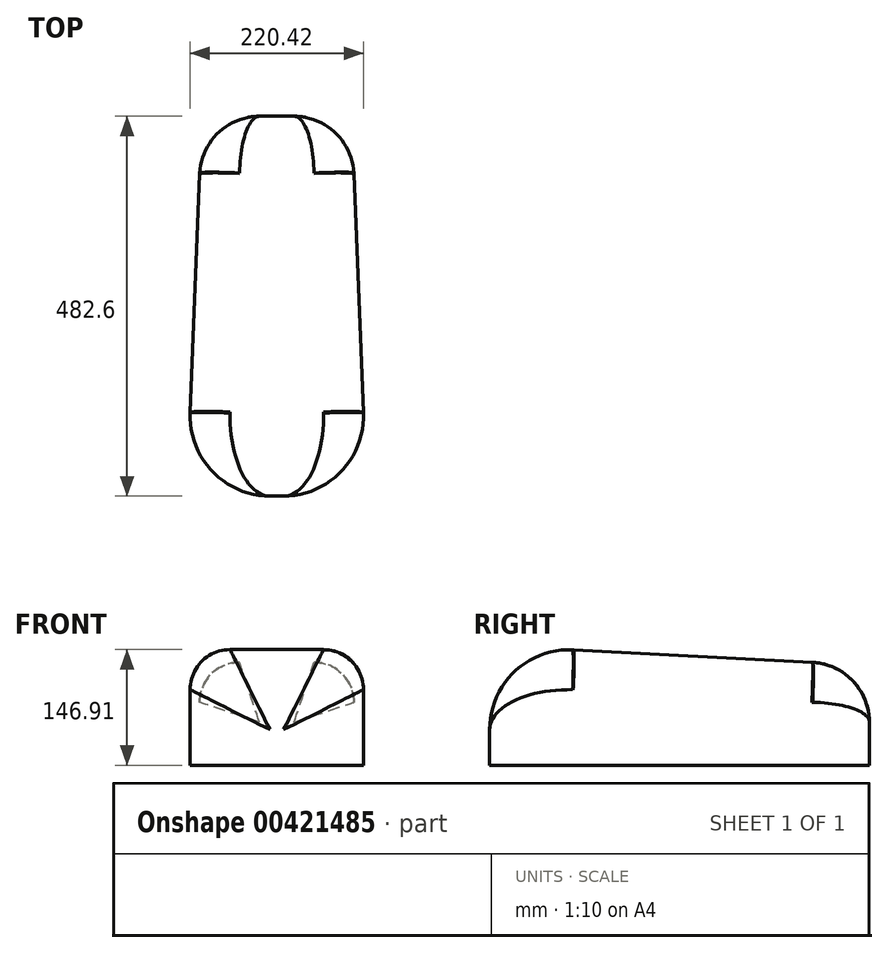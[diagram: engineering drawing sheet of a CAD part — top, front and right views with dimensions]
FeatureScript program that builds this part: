
annotation { "Feature Type Name" : "Feature", "Feature Type Description" : "" }
export const myFeature = defineFeature(function(context is Context, id is Id, definition is map)
    precondition{}
    {
        {
            var Q0;
            Q0=qCreatedBy(makeId("Front.planeOp"),FACE);
            var sketch = newSketch(context, id + "F0", { "sketchPlane" : qUnion([Q0])});
            skLineSegment(sketch, "E0.bottom", {"start": v(-114.3, 152.4) * mm, "end": v(114.3, 152.4) * mm});
            skLineSegment(sketch, "E0.top", {"start": v(-114.3, 0) * mm, "end": v(114.3, 0) * mm});
            skLineSegment(sketch, "E0.left", {"start": v(-114.3, 152.4) * mm, "end": v(-114.3, 0) * mm});
            skLineSegment(sketch, "E0.right", {"start": v(114.3, 152.4) * mm, "end": v(114.3, 0) * mm});
            skSolve(sketch);
        }
        {
            var Q0;
            Q0=qCreatedBy(makeId("Front.planeOp"),FACE);
            cPlane(context, id + "F1", {"entities" : qUnion([Q0]), "cplaneType" : CPlaneType.OFFSET, "offset" : 482.6 * mm, "oppositeDirection" : true, "width" : 152.4 * mm, "height" : 152.4 * mm});
        }
        {
            var Q0;
            Q0=qCreatedBy(id+"F1.planeOp",FACE);
            var sketch = newSketch(context, id + "F2", { "sketchPlane" : qUnion([Q0])});
            skLineSegment(sketch, "E1.bottom", {"start": v(-95.25, 127) * mm, "end": v(95.25, 127) * mm});
            skLineSegment(sketch, "E1.top", {"start": v(-95.25, 0) * mm, "end": v(95.25, 0) * mm});
            skLineSegment(sketch, "E1.left", {"start": v(-95.25, 127) * mm, "end": v(-95.25, 0) * mm});
            skLineSegment(sketch, "E1.right", {"start": v(95.25, 127) * mm, "end": v(95.25, 0) * mm});
            skSolve(sketch);
        }
        {
            var Q0;
            Q0 = qSketchRegion(id + "F0", true);
            var Q1;
            Q1 = qSketchRegion(id + "F2", true);
            loft(context, id + "F3", {"sheetProfilesArray" : [{ "sheetProfileEntities" : qUnion([Q0]) }, { "sheetProfileEntities" : qUnion([Q1]) }]});
        }
        {
            var Q0;
            Q0=makeQuery(id+"F3.opLoft","SWEPT_EDGE",EDGE,{"disambiguationData":[OSD([sQuery(id+"F0.wireOp",EDGE,"E0.bottom"),sQuery(id+"F0.wireOp",EDGE,"E0.right"),sQuery(id+"F2.wireOp",EDGE,"E1.bottom"),sQuery(id+"F2.wireOp",EDGE,"E1.right")])]});
            var Q1;
            Q1=makeQuery(id+"F3.opLoft","SWEPT_EDGE",EDGE,{"disambiguationData":[OSD([sQuery(id+"F0.wireOp",EDGE,"E0.bottom"),sQuery(id+"F0.wireOp",EDGE,"E0.left"),sQuery(id+"F2.wireOp",EDGE,"E1.bottom"),sQuery(id+"F2.wireOp",EDGE,"E1.left")])]});
            fillet(context, id + "F4", {"entities" : qUnion([Q0, Q1]), "radius" : 50.8 * mm, "tangentPropagation" : true, "allowEdgeOverflow" : false});
        }
        {
            var Q0;
            Q0=makeQuery(id+"F3.opLoft","MID_CAP_EDGE",EDGE,{"disambiguationData":[OSD([sQuery(id+"F0.wireOp",EDGE,"E0.bottom"),sQuery(id+"F0.wireOp",EDGE,"E0.top"),sQuery(id+"F0.wireOp",EDGE,"E0.right")])],"capPos":0.0});
            var Q1;
            {var subQ0=sQuery(id+"F0.wireOp",EDGE,"E0.bottom");var subQ1=sQuery(id+"F0.wireOp",EDGE,"E0.right");Q1=makeQuery(id+"F4.opFillet","BLEND_EDGE",EDGE,{"blendedFrom":[makeQuery(id+"F3.opLoft","SWEPT_EDGE",EDGE,{"disambiguationData":[OSD([subQ0,subQ1,sQuery(id+"F2.wireOp",EDGE,"E1.bottom"),sQuery(id+"F2.wireOp",EDGE,"E1.right")])]}),makeQuery(id+"F3.opLoft","CAP_FACE",FACE,{"disambiguationData":[OSD([makeQuery(id+"F0.imprint","IMPRINT",FACE,{"disambiguationData":[TD([[makeQuery(id+"F0.imprint","IMPRINT",EDGE,{"derivedFrom":subQ0}),-1.0]])]})])],"isStart":true})],"blendedInto":[makeQuery(id+"F3.opLoft","CAP_FACE",FACE,{"disambiguationData":[OSD([makeQuery(id+"F0.imprint","IMPRINT",FACE,{"disambiguationData":[TD([[makeQuery(id+"F0.imprint","IMPRINT",EDGE,{"derivedFrom":subQ0}),-1.0]])]})])],"isStart":true})]});}
            var Q2;
            Q2=makeQuery(id+"F3.opLoft","MID_CAP_EDGE",EDGE,{"disambiguationData":[OSD([sQuery(id+"F0.wireOp",EDGE,"E0.bottom"),sQuery(id+"F0.wireOp",EDGE,"E0.left"),sQuery(id+"F0.wireOp",EDGE,"E0.right")])],"capPos":0.0});
            var Q3;
            {var subQ0=sQuery(id+"F0.wireOp",EDGE,"E0.bottom");var subQ1=sQuery(id+"F0.wireOp",EDGE,"E0.left");Q3=makeQuery(id+"F4.opFillet","BLEND_EDGE",EDGE,{"blendedFrom":[makeQuery(id+"F3.opLoft","SWEPT_EDGE",EDGE,{"disambiguationData":[OSD([subQ0,subQ1,sQuery(id+"F2.wireOp",EDGE,"E1.bottom"),sQuery(id+"F2.wireOp",EDGE,"E1.left")])]}),makeQuery(id+"F3.opLoft","CAP_FACE",FACE,{"disambiguationData":[OSD([makeQuery(id+"F0.imprint","IMPRINT",FACE,{"disambiguationData":[TD([[makeQuery(id+"F0.imprint","IMPRINT",EDGE,{"derivedFrom":subQ0}),-1.0]])]})])],"isStart":true})],"blendedInto":[makeQuery(id+"F3.opLoft","CAP_FACE",FACE,{"disambiguationData":[OSD([makeQuery(id+"F0.imprint","IMPRINT",FACE,{"disambiguationData":[TD([[makeQuery(id+"F0.imprint","IMPRINT",EDGE,{"derivedFrom":subQ0}),-1.0]])]})])],"isStart":true})]});}
            var Q4;
            Q4=makeQuery(id+"F3.opLoft","MID_CAP_EDGE",EDGE,{"disambiguationData":[OSD([sQuery(id+"F0.wireOp",EDGE,"E0.bottom"),sQuery(id+"F0.wireOp",EDGE,"E0.top"),sQuery(id+"F0.wireOp",EDGE,"E0.left")])],"capPos":0.0});
            fillet(context, id + "F5", {"entities" : qUnion([Q0, Q1, Q2, Q3, Q4]), "radius" : 101.6 * mm, "tangentPropagation" : true, "allowEdgeOverflow" : false});
        }
        {
            var Q0;
            Q0=makeQuery(id+"F3.opLoft","MID_CAP_EDGE",EDGE,{"disambiguationData":[OSD([sQuery(id+"F2.wireOp",EDGE,"E1.bottom"),sQuery(id+"F2.wireOp",EDGE,"E1.top"),sQuery(id+"F2.wireOp",EDGE,"E1.right")])],"capPos":1.0});
            var Q1;
            {var subQ0=sQuery(id+"F2.wireOp",EDGE,"E1.bottom");var subQ1=sQuery(id+"F2.wireOp",EDGE,"E1.right");Q1=makeQuery(id+"F4.opFillet","BLEND_EDGE",EDGE,{"blendedFrom":[makeQuery(id+"F3.opLoft","SWEPT_EDGE",EDGE,{"disambiguationData":[OSD([sQuery(id+"F0.wireOp",EDGE,"E0.bottom"),sQuery(id+"F0.wireOp",EDGE,"E0.right"),subQ0,subQ1])]}),makeQuery(id+"F3.opLoft","CAP_FACE",FACE,{"disambiguationData":[OSD([makeQuery(id+"F2.imprint","IMPRINT",FACE,{"disambiguationData":[TD([[makeQuery(id+"F2.imprint","IMPRINT",EDGE,{"derivedFrom":subQ0}),-1.0]])]})])],"isStart":true})],"blendedInto":[makeQuery(id+"F3.opLoft","CAP_FACE",FACE,{"disambiguationData":[OSD([makeQuery(id+"F2.imprint","IMPRINT",FACE,{"disambiguationData":[TD([[makeQuery(id+"F2.imprint","IMPRINT",EDGE,{"derivedFrom":subQ0}),-1.0]])]})])],"isStart":true})]});}
            var Q2;
            Q2=makeQuery(id+"F3.opLoft","MID_CAP_EDGE",EDGE,{"disambiguationData":[OSD([sQuery(id+"F2.wireOp",EDGE,"E1.bottom"),sQuery(id+"F2.wireOp",EDGE,"E1.left"),sQuery(id+"F2.wireOp",EDGE,"E1.right")])],"capPos":1.0});
            var Q3;
            {var subQ0=sQuery(id+"F2.wireOp",EDGE,"E1.bottom");var subQ1=sQuery(id+"F2.wireOp",EDGE,"E1.left");Q3=makeQuery(id+"F4.opFillet","BLEND_EDGE",EDGE,{"blendedFrom":[makeQuery(id+"F3.opLoft","SWEPT_EDGE",EDGE,{"disambiguationData":[OSD([sQuery(id+"F0.wireOp",EDGE,"E0.bottom"),sQuery(id+"F0.wireOp",EDGE,"E0.left"),subQ0,subQ1])]}),makeQuery(id+"F3.opLoft","CAP_FACE",FACE,{"disambiguationData":[OSD([makeQuery(id+"F2.imprint","IMPRINT",FACE,{"disambiguationData":[TD([[makeQuery(id+"F2.imprint","IMPRINT",EDGE,{"derivedFrom":subQ0}),-1.0]])]})])],"isStart":true})],"blendedInto":[makeQuery(id+"F3.opLoft","CAP_FACE",FACE,{"disambiguationData":[OSD([makeQuery(id+"F2.imprint","IMPRINT",FACE,{"disambiguationData":[TD([[makeQuery(id+"F2.imprint","IMPRINT",EDGE,{"derivedFrom":subQ0}),-1.0]])]})])],"isStart":true})]});}
            var Q4;
            Q4=makeQuery(id+"F3.opLoft","MID_CAP_EDGE",EDGE,{"disambiguationData":[OSD([sQuery(id+"F2.wireOp",EDGE,"E1.bottom"),sQuery(id+"F2.wireOp",EDGE,"E1.top"),sQuery(id+"F2.wireOp",EDGE,"E1.left")])],"capPos":1.0});
            fillet(context, id + "F6", {"entities" : qUnion([Q0, Q1, Q2, Q3, Q4]), "radius" : 76.2 * mm, "tangentPropagation" : true, "allowEdgeOverflow" : false});
        }
    });
